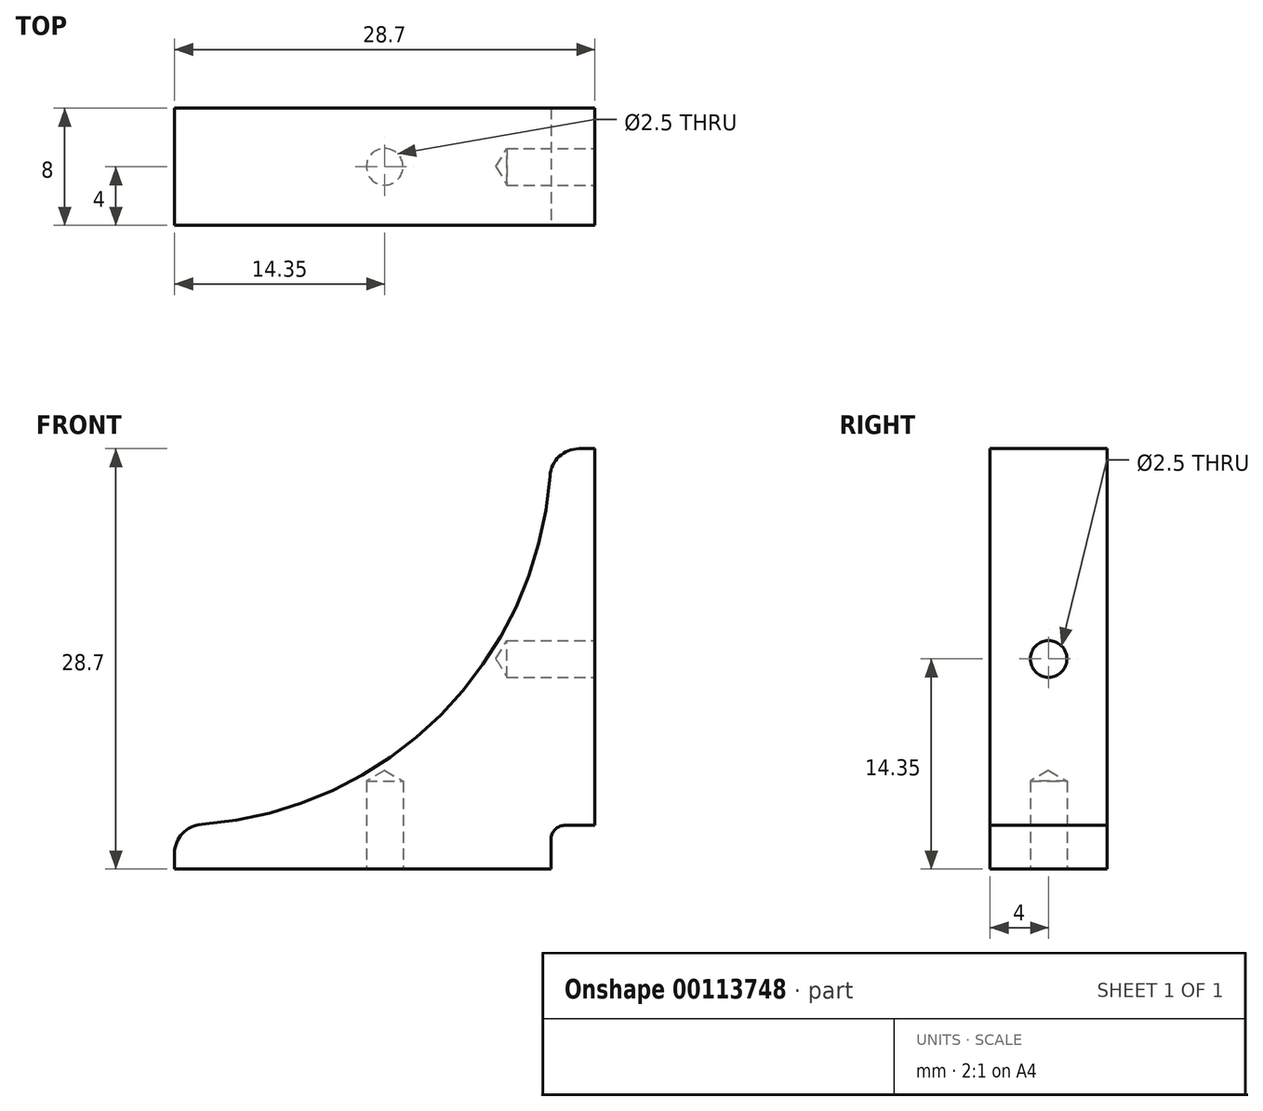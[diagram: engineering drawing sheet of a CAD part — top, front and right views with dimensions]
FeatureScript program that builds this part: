
annotation { "Feature Type Name" : "Feature", "Feature Type Description" : "" }
export const myFeature = defineFeature(function(context is Context, id is Id, definition is map)
    precondition{}
    {
        {
            var Q0;
            Q0=qCreatedBy(makeId("Front.planeOp"),FACE);
            var sketch = newSketch(context, id + "F0", { "sketchPlane" : qUnion([Q0])});
            skLineSegment(sketch, "E0", {"start": v(0, 0) * mm, "end": v(-28.7, 0) * mm});
            skLineSegment(sketch, "E1", {"start": v(-28.7, 0) * mm, "end": v(-28.7, 3) * mm});
            skLineSegment(sketch, "E2", {"start": v(0, 0) * mm, "end": v(0, 28.7) * mm});
            skLineSegment(sketch, "E3", {"start": v(0, 28.7) * mm, "end": v(-3, 28.7) * mm});
            skArc(sketch, "E4", {"start": v(-28.7, 3) * mm, "mid": v(-10.53, 10.53) * mm, "end": v(-3, 28.7) * mm});
            skSolve(sketch);
        }
        {
            var Q0;
            Q0=makeQuery(id+"F0.imprint","IMPRINT",FACE,{"disambiguationData":[TD([[makeQuery(id+"F0.imprint","IMPRINT",EDGE,{"derivedFrom":sQuery(id+"F0.wireOp",EDGE,"E0")}),-1.0]])]});
            extrude(context, id + "F1", {"entities" : qUnion([Q0]), "depth" : 8 * mm});
        }
        {
            var Q0;
            Q0=makeQuery(id+"F1.opExtrude","SWEPT_FACE",FACE,{"disambiguationData":[OSD([sQuery(id+"F0.wireOp",EDGE,"E2")])]});
            var sketch = newSketch(context, id + "F2", { "sketchPlane" : qUnion([Q0])});
            skLineSegment(sketch, "E5", {"start": v(-4, 28.7) * mm, "end": v(-4, 0) * mm, "construction": true});
            skPoint(sketch, "E6", {"position": v(-4, 14.35) * mm});
            skSolve(sketch);
        }
        {
            var Q0;
            Q0=sQuery(id+"F2.wireOp",VERTEX,"E6");
            var Q1;
            Q1=makeQuery(id+"F1.opExtrude","SWEPT_BODY",BODY,{"disambiguationData":[OSD([sQuery(id+"F0.wireOp",EDGE,"E0"),sQuery(id+"F0.wireOp",EDGE,"E1"),sQuery(id+"F0.wireOp",EDGE,"E2"),sQuery(id+"F0.wireOp",EDGE,"E3"),sQuery(id+"F0.wireOp",EDGE,"E4")])]});
            hole(context, id + "F3", {"style" : HoleStyle.SIMPLE, "endStyle" : HoleEndStyle.BLIND, "holeDiameter" : 2.5 * mm, "holeDepth" : 6 * mm, "locations" : qUnion([Q0]), "scope" : qUnion([Q1])});
        }
        {
            var Q0;
            Q0=makeQuery(id+"F1.opExtrude","SWEPT_FACE",FACE,{"disambiguationData":[OSD([sQuery(id+"F0.wireOp",EDGE,"E0")])]});
            var sketch = newSketch(context, id + "F4", { "sketchPlane" : qUnion([Q0])});
            skLineSegment(sketch, "E7", {"start": v(-28.7, 4) * mm, "end": v(0, 4) * mm, "construction": true});
            skPoint(sketch, "E8", {"position": v(-14.35, 4) * mm});
            skSolve(sketch);
        }
        {
            var Q0;
            Q0=sQuery(id+"F4.wireOp",VERTEX,"E8");
            var Q1;
            Q1=makeQuery(id+"F1.opExtrude","SWEPT_BODY",BODY,{"disambiguationData":[OSD([sQuery(id+"F0.wireOp",EDGE,"E0"),sQuery(id+"F0.wireOp",EDGE,"E1"),sQuery(id+"F0.wireOp",EDGE,"E2"),sQuery(id+"F0.wireOp",EDGE,"E3"),sQuery(id+"F0.wireOp",EDGE,"E4")])]});
            hole(context, id + "F5", {"style" : HoleStyle.SIMPLE, "endStyle" : HoleEndStyle.BLIND, "holeDiameter" : 2.5 * mm, "holeDepth" : 6 * mm, "locations" : qUnion([Q0]), "scope" : qUnion([Q1])});
        }
        {
            var Q0;
            Q0=makeQuery(id+"F1.opExtrude","SWEPT_EDGE",EDGE,{"disambiguationData":[OSD([sQuery(id+"F0.wireOp",EDGE,"E3"),sQuery(id+"F0.wireOp",EDGE,"E4")])]});
            var Q1;
            Q1=makeQuery(id+"F1.opExtrude","SWEPT_EDGE",EDGE,{"disambiguationData":[OSD([sQuery(id+"F0.wireOp",EDGE,"E1"),sQuery(id+"F0.wireOp",EDGE,"E4")])]});
            fillet(context, id + "F6", {"entities" : qUnion([Q0, Q1]), "radius" : 2 * mm, "tangentPropagation" : true, "allowEdgeOverflow" : false});
        }
        {
            var Q0;
            Q0=makeQuery(id+"F1.opExtrude","CAP_FACE",FACE,{"disambiguationData":[OSD([sQuery(id+"F0.wireOp",EDGE,"E0"),sQuery(id+"F0.wireOp",EDGE,"E1"),sQuery(id+"F0.wireOp",EDGE,"E2"),sQuery(id+"F0.wireOp",EDGE,"E3"),sQuery(id+"F0.wireOp",EDGE,"E4")])],"isStart":false});
            var sketch = newSketch(context, id + "F7", { "sketchPlane" : qUnion([Q0])});
            skLineSegment(sketch, "E9.bottom", {"start": v(0, 0) * mm, "end": v(-3, 0) * mm});
            skLineSegment(sketch, "E9.top", {"start": v(0, 3) * mm, "end": v(-3, 3) * mm});
            skLineSegment(sketch, "E9.left", {"start": v(0, 0) * mm, "end": v(0, 3) * mm});
            skLineSegment(sketch, "E9.right", {"start": v(-3, 0) * mm, "end": v(-3, 3) * mm});
            skSolve(sketch);
        }
        {
            var Q0;
            Q0=makeQuery(id+"F7.imprint","IMPRINT",FACE,{"disambiguationData":[TD([[makeQuery(id+"F7.imprint","IMPRINT",EDGE,{"derivedFrom":sQuery(id+"F7.wireOp",EDGE,"E9.bottom")}),-1.0]])]});
            extrude(context, id + "F8", {"entities" : qUnion([Q0]), "operationType" : NewBodyOperationType.REMOVE, "endBound" : BoundingType.THROUGH_ALL, "oppositeDirection" : true, "depth" : 25 * mm});
        }
        {
            var Q0;
            Q0=makeQuery(id+"F8.boolean.opBoolean","COPY",EDGE,{"derivedFrom":makeQuery(id+"F8.opExtrude","SWEPT_EDGE",EDGE,{"disambiguationData":[OSD([sQuery(id+"F0.wireOp",EDGE,"E2"),sQuery(id+"F7.wireOp",EDGE,"E9.top"),sQuery(id+"F7.wireOp",EDGE,"E9.left")])]})});
            var Q1;
            Q1=makeQuery(id+"F8.boolean.opBoolean","COPY",EDGE,{"derivedFrom":makeQuery(id+"F8.opExtrude","SWEPT_EDGE",EDGE,{"disambiguationData":[OSD([sQuery(id+"F7.wireOp",EDGE,"E9.top"),sQuery(id+"F7.wireOp",EDGE,"E9.right")])]})});
            var Q2;
            Q2=makeQuery(id+"F8.boolean.opBoolean","COPY",EDGE,{"derivedFrom":makeQuery(id+"F8.opExtrude","SWEPT_EDGE",EDGE,{"disambiguationData":[OSD([sQuery(id+"F0.wireOp",EDGE,"E0"),sQuery(id+"F7.wireOp",EDGE,"E9.bottom"),sQuery(id+"F7.wireOp",EDGE,"E9.right")])]})});
            fillet(context, id + "F9", {"entities" : qUnion([Q0, Q1, Q2]), "radius" : 1 * mm, "tangentPropagation" : true, "allowEdgeOverflow" : false});
        }
    });
